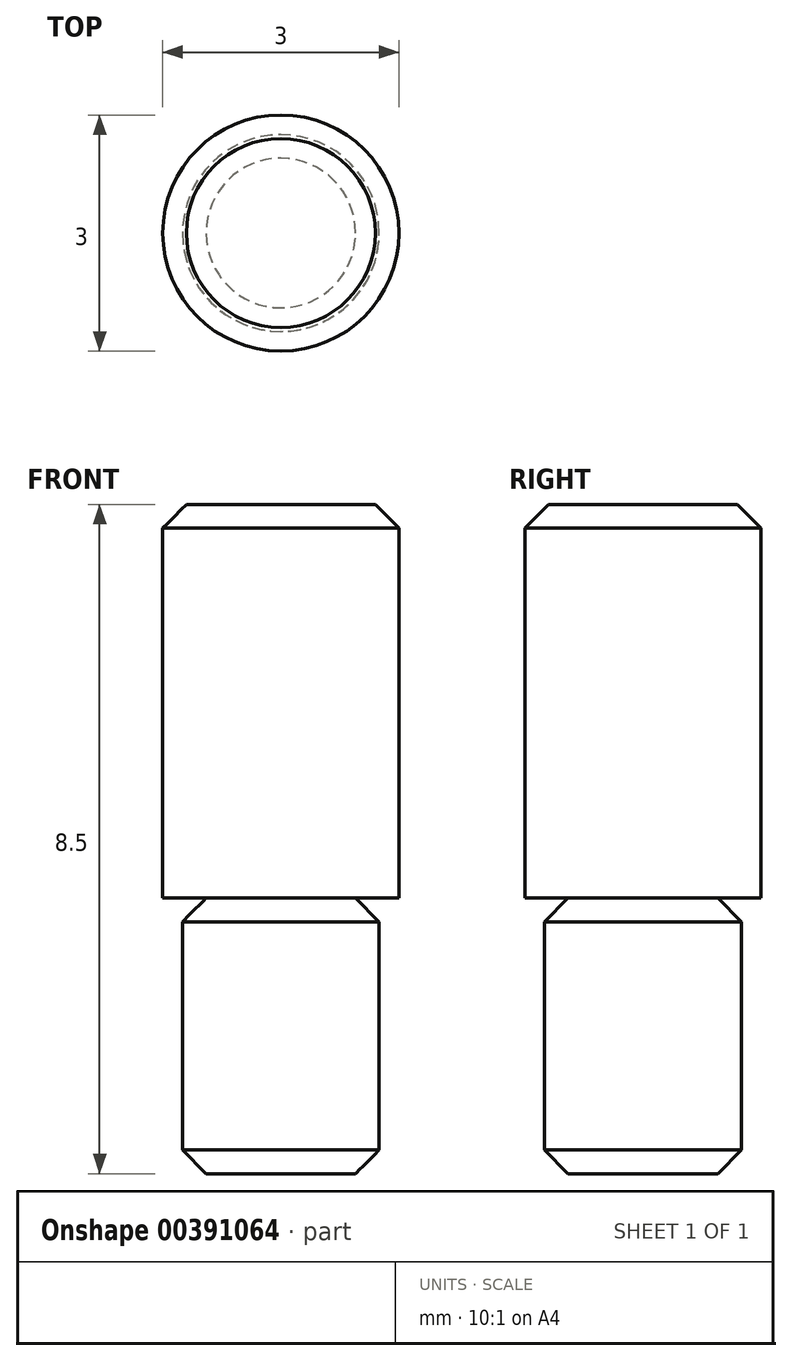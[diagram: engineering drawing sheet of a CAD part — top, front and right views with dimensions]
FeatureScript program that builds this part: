
annotation { "Feature Type Name" : "Feature", "Feature Type Description" : "" }
export const myFeature = defineFeature(function(context is Context, id is Id, definition is map)
    precondition{}
    {
        {
            var Q0;
            Q0=qCreatedBy(makeId("Front.planeOp"),FACE);
            var sketch = newSketch(context, id + "F0", { "sketchPlane" : qUnion([Q0])});
            skLineSegment(sketch, "E0", {"start": v(0, 0) * mm, "end": v(0, 5) * mm});
            skLineSegment(sketch, "E1", {"start": v(0, 5) * mm, "end": v(1.5, 5) * mm});
            skLineSegment(sketch, "E2", {"start": v(1.5, 5) * mm, "end": v(1.5, 0) * mm});
            skLineSegment(sketch, "E3", {"start": v(1.5, 0) * mm, "end": v(1.25, 0) * mm});
            skLineSegment(sketch, "E4", {"start": v(1.25, -0.3) * mm, "end": v(1.25, -3.5) * mm});
            skLineSegment(sketch, "E5", {"start": v(1.25, -3.5) * mm, "end": v(0, -3.5) * mm});
            skLineSegment(sketch, "E6", {"start": v(0, -3.5) * mm, "end": v(0, 0) * mm});
            skLineSegment(sketch, "E7", {"start": v(1.25, -0.3) * mm, "end": v(0.95, 0) * mm});
            skLineSegment(sketch, "E8", {"start": v(0.95, 0) * mm, "end": v(1.25, 0) * mm});
            skSolve(sketch);
        }
        {
            var Q0;
            Q0=makeQuery(id+"F0.imprint","IMPRINT",FACE,{"disambiguationData":[TD([[makeQuery(id+"F0.imprint","IMPRINT",EDGE,{"derivedFrom":sQuery(id+"F0.wireOp",EDGE,"E0")}),-1.0]])]});
            var Q1;
            Q1=sQuery(id+"F0.wireOp",EDGE,"E6");
            revolve(context, id + "F1", {"entities" : qUnion([Q0]), "axis" : qUnion([Q1]), "revolveType" : RevolveType.FULL});
        }
        {
            var Q0;
            Q0=makeQuery(id+"F1.opRevolve","SWEPT_EDGE",EDGE,{"disambiguationData":[OSD([sQuery(id+"F0.wireOp",EDGE,"E1"),sQuery(id+"F0.wireOp",EDGE,"E2")])]});
            var Q1;
            Q1=makeQuery(id+"F1.opRevolve","SWEPT_EDGE",EDGE,{"disambiguationData":[OSD([sQuery(id+"F0.wireOp",EDGE,"E4"),sQuery(id+"F0.wireOp",EDGE,"E5")])]});
            chamfer(context, id + "F2", {"entities" : qUnion([Q0, Q1]), "width" : 0.3 * mm});
        }
    });
